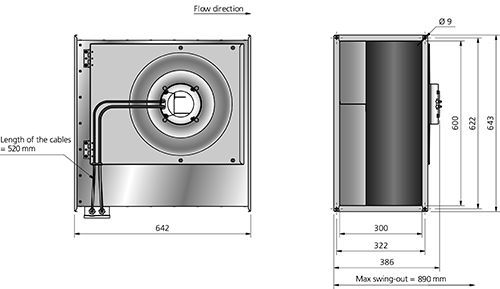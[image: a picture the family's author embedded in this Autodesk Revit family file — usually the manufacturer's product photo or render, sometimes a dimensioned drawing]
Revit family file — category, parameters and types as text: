
# Revit family: RKB 600X300 E3 EC_7480102
name_source: partatom
category: Mechanical Equipment
revit_build: Autodesk Revit MEP 2014 (Build: 20130308_1515(x64)
units: mm (PartAtom-declared; Revit-internal decimal feet)

## types (1)
- RBK 600X300 E3 EC
    Capacitor = - μF
    Connector Height = 300 mm
    Connector Width = 600 mm
    Current = 2 A
    Depth = 643 mm  [stored 2.10958 ft]
    Description = UNINSULATED DUCT FANS WITH RECTANGULAR CONNECTIONS
    Frequency = 50 Hz
    Height = 391 mm
    Main Material = Steel, Galvanized
    Max. temperature of transported air = 60 °C
    Max. temperature of transported air when speed controlled = 60 °C
    Phase = 3
    Power = 1220 W
    Sound pressure level at 3 m = 71 dB(A)
    Speed = 2500 rpm
    Voltage = 400 V
    Voltage range = 380-480 V
    Weight = 29.10 kg
    Width = 642 mm  [stored 2.1063 ft]
    Wiring diagram = 4040147

note: [stored X ft] marks values corroborated as IEEE doubles in the binary element streams (Revit-internal decimal feet)

## geometry (parser evidence)
native form markers: Sweep x4
no freeform markers — native parametric forms only
